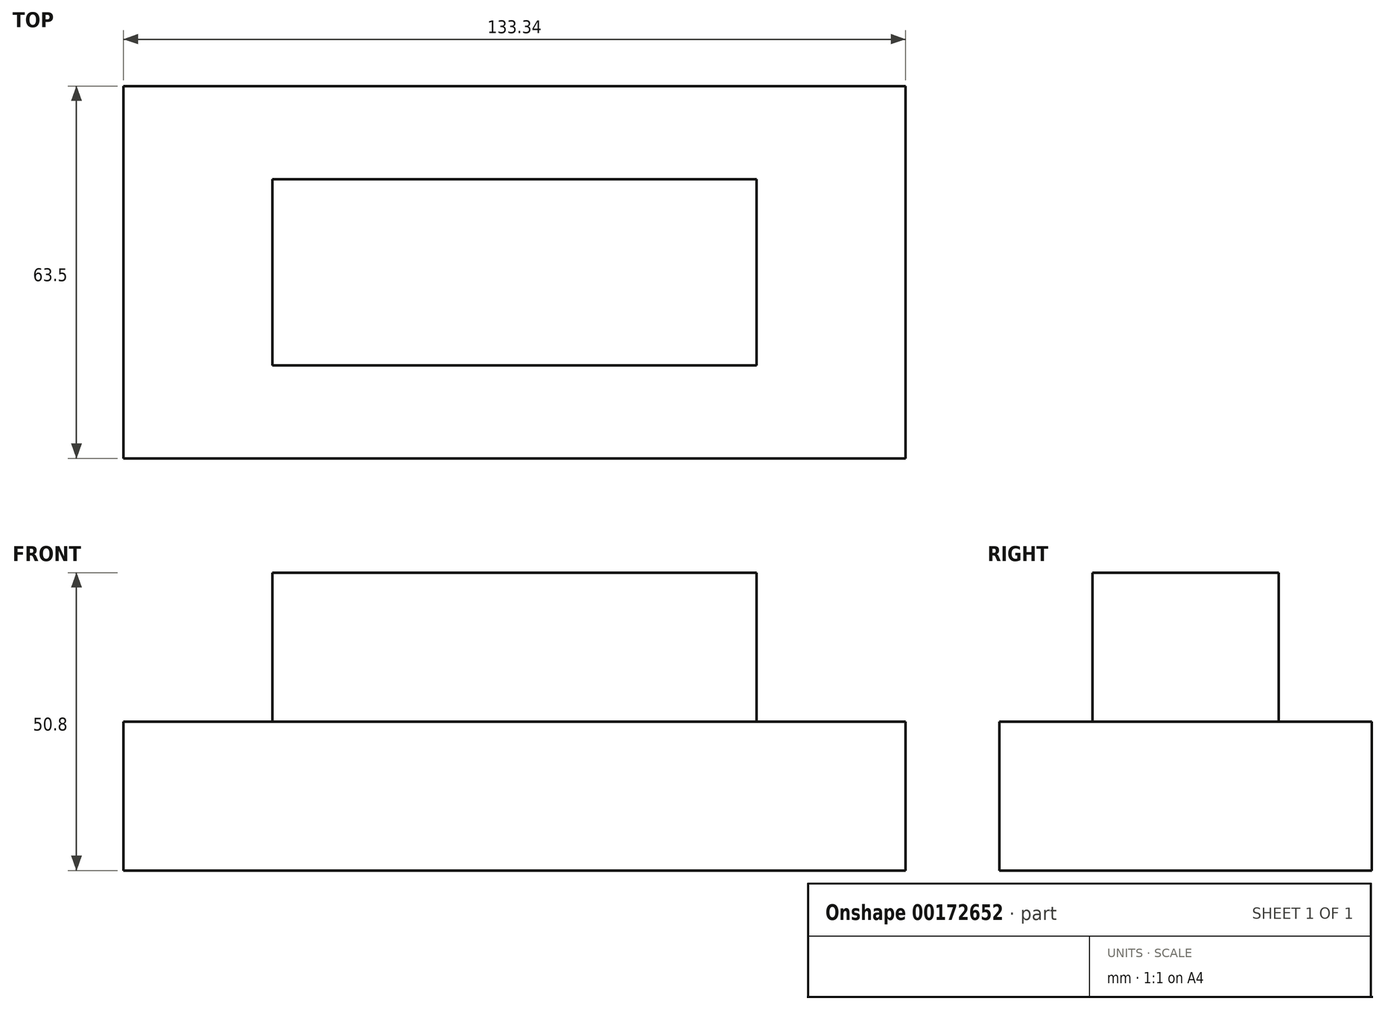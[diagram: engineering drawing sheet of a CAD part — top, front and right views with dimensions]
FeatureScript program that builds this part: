
annotation { "Feature Type Name" : "Feature", "Feature Type Description" : "" }
export const myFeature = defineFeature(function(context is Context, id is Id, definition is map)
    precondition{}
    {
        {
            var Q0;
            Q0=qCreatedBy(makeId("Top.planeOp"),FACE);
            var sketch = newSketch(context, id + "F0", { "sketchPlane" : qUnion([Q0])});
            skLineSegment(sketch, "E0.bottom", {"start": v(66.68, 31.75) * mm, "end": v(-66.68, 31.75) * mm});
            skLineSegment(sketch, "E0.top", {"start": v(66.68, -31.75) * mm, "end": v(-66.68, -31.75) * mm});
            skLineSegment(sketch, "E0.left", {"start": v(66.68, 31.75) * mm, "end": v(66.68, -31.75) * mm});
            skLineSegment(sketch, "E0.right", {"start": v(-66.68, 31.75) * mm, "end": v(-66.68, -31.75) * mm});
            skPoint(sketch, "E0.middle", {"position": v(0, 0) * mm});
            skLineSegment(sketch, "E1.bottom", {"start": v(41.28, 15.88) * mm, "end": v(-41.28, 15.88) * mm});
            skLineSegment(sketch, "E1.top", {"start": v(41.28, -15.88) * mm, "end": v(-41.28, -15.88) * mm});
            skLineSegment(sketch, "E1.left", {"start": v(41.28, 15.88) * mm, "end": v(41.28, -15.88) * mm});
            skLineSegment(sketch, "E1.right", {"start": v(-41.28, 15.88) * mm, "end": v(-41.28, -15.88) * mm});
            skSolve(sketch);
        }
        {
            var Q0;
            Q0 = qSketchRegion(id + "F0", true);
            extrude(context, id + "F1", {"entities" : qUnion([Q0]), "depth" : 25.4 * mm});
        }
        {
            var Q0;
            Q0=qCreatedBy(makeId("Top.planeOp"),FACE);
            var sketch = newSketch(context, id + "F2", { "sketchPlane" : qUnion([Q0])});
            skLineSegment(sketch, "E2.bottom", {"start": v(41.28, 15.88) * mm, "end": v(-41.28, 15.88) * mm});
            skLineSegment(sketch, "E2.top", {"start": v(41.28, -15.88) * mm, "end": v(-41.28, -15.88) * mm});
            skLineSegment(sketch, "E2.left", {"start": v(41.28, 15.88) * mm, "end": v(41.28, -15.88) * mm});
            skLineSegment(sketch, "E2.right", {"start": v(-41.28, 15.88) * mm, "end": v(-41.28, -15.88) * mm});
            skPoint(sketch, "E2.middle", {"position": v(0, 0) * mm});
            skSolve(sketch);
        }
        {
            var Q0;
            Q0 = qSketchRegion(id + "F2", true);
            extrude(context, id + "F3", {"entities" : qUnion([Q0]), "operationType" : NewBodyOperationType.ADD, "depth" : 50.8 * mm});
        }
    });
